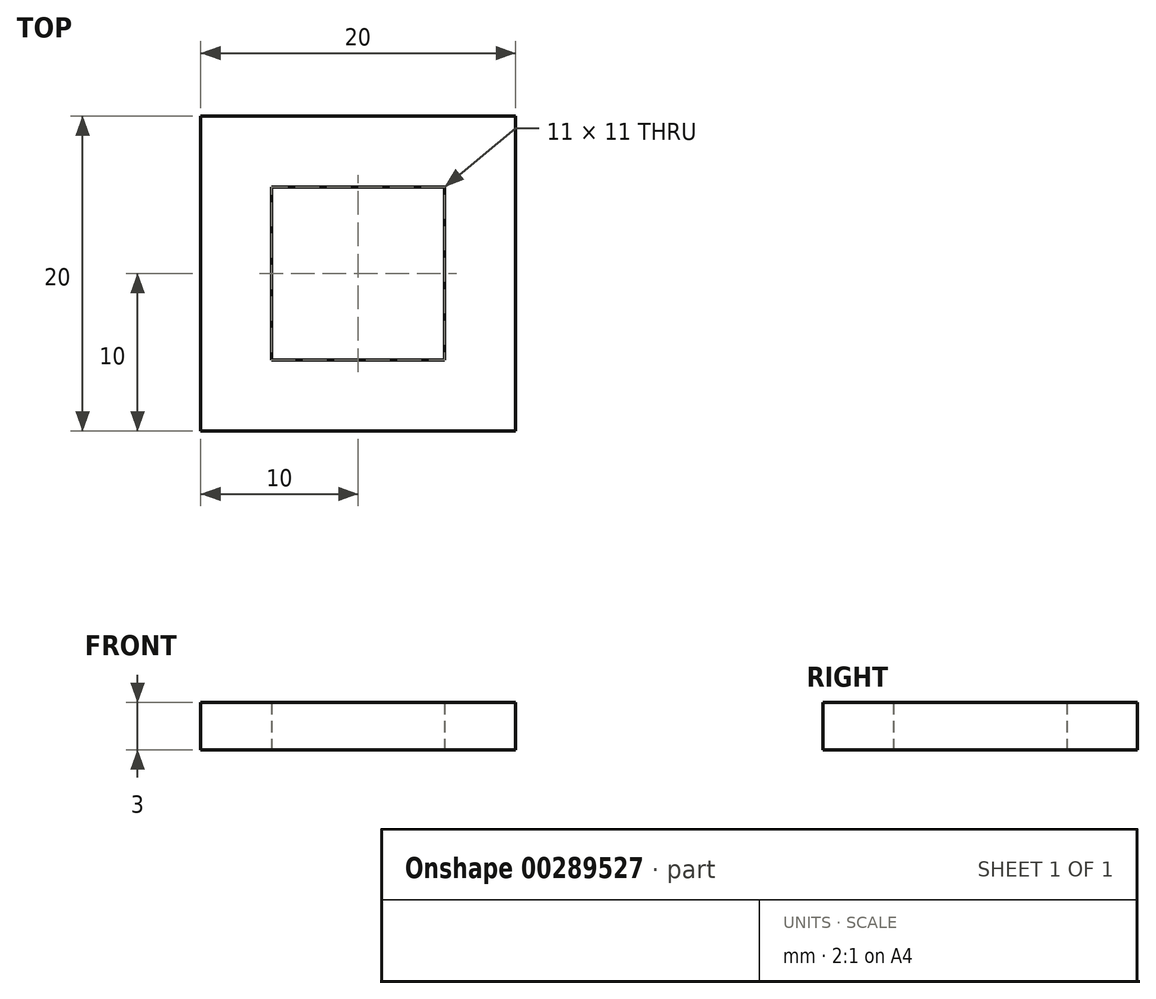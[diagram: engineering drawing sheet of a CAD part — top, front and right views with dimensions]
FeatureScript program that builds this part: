
annotation { "Feature Type Name" : "Feature", "Feature Type Description" : "" }
export const myFeature = defineFeature(function(context is Context, id is Id, definition is map)
    precondition{}
    {
        {
            var Q0;
            Q0=qCreatedBy(makeId("Top.planeOp"),FACE);
            var sketch = newSketch(context, id + "F0", { "sketchPlane" : qUnion([Q0])});
            skLineSegment(sketch, "E0.bottom", {"start": v(10, 10) * mm, "end": v(-10, 10) * mm});
            skLineSegment(sketch, "E0.top", {"start": v(10, -10) * mm, "end": v(-10, -10) * mm});
            skLineSegment(sketch, "E0.left", {"start": v(10, 10) * mm, "end": v(10, -10) * mm});
            skLineSegment(sketch, "E0.right", {"start": v(-10, 10) * mm, "end": v(-10, -10) * mm});
            skPoint(sketch, "E0.middle", {"position": v(0, 0) * mm});
            skLineSegment(sketch, "E1.bottom", {"start": v(5, 5) * mm, "end": v(-5, 5) * mm});
            skLineSegment(sketch, "E1.top", {"start": v(5, -5) * mm, "end": v(-5, -5) * mm});
            skLineSegment(sketch, "E1.left", {"start": v(5, 5) * mm, "end": v(5, -5) * mm});
            skLineSegment(sketch, "E1.right", {"start": v(-5, 5) * mm, "end": v(-5, -5) * mm});
            skLineSegment(sketch, "E2.bottom", {"start": v(5.5, 5.5) * mm, "end": v(-5.5, 5.5) * mm});
            skLineSegment(sketch, "E2.top", {"start": v(5.5, -5.5) * mm, "end": v(-5.5, -5.5) * mm});
            skLineSegment(sketch, "E2.left", {"start": v(5.5, 5.5) * mm, "end": v(5.5, -5.5) * mm});
            skLineSegment(sketch, "E2.right", {"start": v(-5.5, 5.5) * mm, "end": v(-5.5, -5.5) * mm});
            skSolve(sketch);
        }
        {
            var Q0;
            Q0=makeQuery(id+"F0.imprint","IMPRINT",FACE,{"disambiguationData":[TD([[makeQuery(id+"F0.imprint","IMPRINT",EDGE,{"derivedFrom":sQuery(id+"F0.wireOp",EDGE,"E0.bottom")}),1.0]])]});
            extrude(context, id + "F1", {"entities" : qUnion([Q0]), "depth" : 3 * mm});
        }
    });
